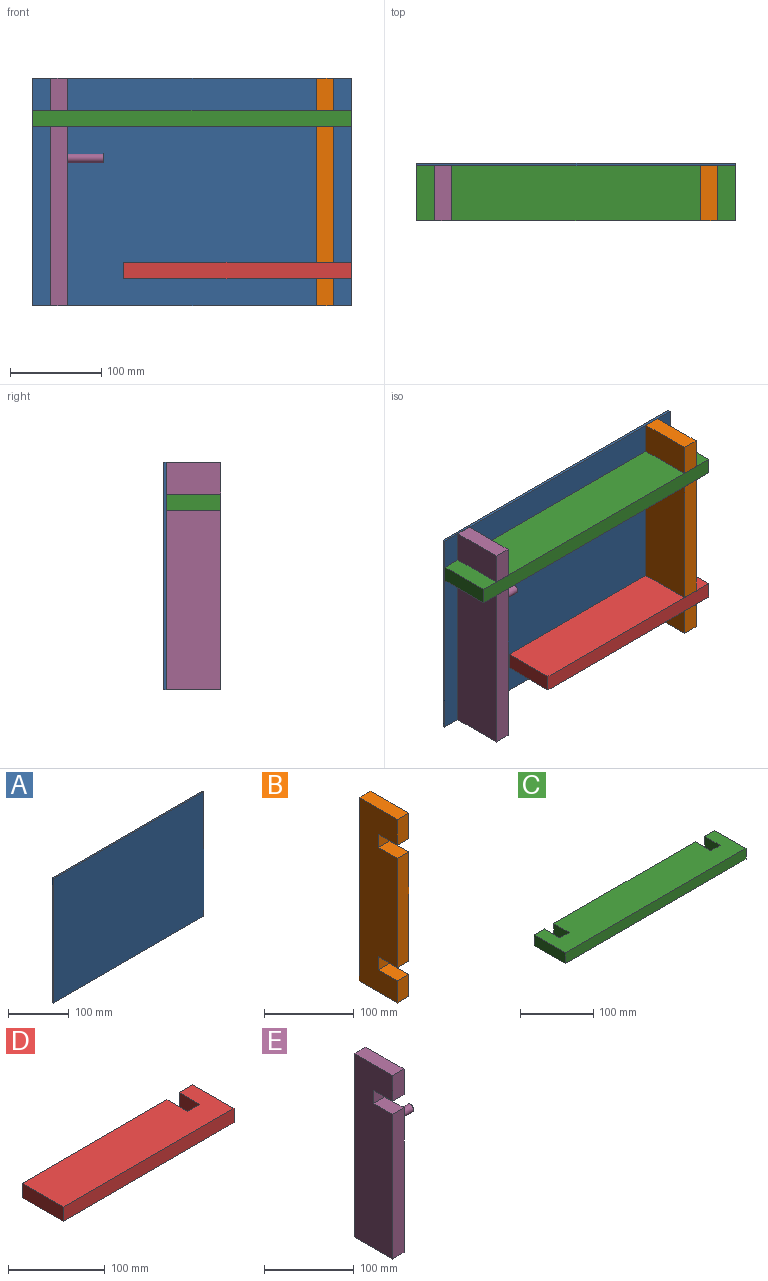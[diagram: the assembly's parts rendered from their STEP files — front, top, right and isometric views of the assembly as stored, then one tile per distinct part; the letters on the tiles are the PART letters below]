
ASSEMBLY  parts=5 mates=4
PART A: 6 faces, bbox 350x3x250 mm
  f0: plane 350x3mm, normal (0,0,1), area 1050mm2, adj f1,f3,f4,f5
  f1: plane 250x3mm, normal (-1,0,0), area 750mm2, adj f0,f2,f4,f5
  f2: plane 350x3mm, normal (0,0,-1), area 1050mm2, adj f1,f3,f4,f5
  f3: plane 250x3mm, normal (1,0,0), area 750mm2, adj f0,f2,f4,f5
  f4: plane 350x250mm, normal (0,-1,0), area 87500mm2, adj f0,f1,f2,f3
  f5: plane 350x250mm, normal (0,1,0), area 87500mm2, adj f0,f1,f2,f3
PART B: 14 faces, bbox 18x60x250 mm
  f0: plane 149x18mm, normal (0,-1,0), area 2682mm2, adj f1,f2,f9,f11
  f1: plane 250x60mm, normal (-1,0,0), area 13920mm2, adj f0,f3,f4,f5,f6,f7,f8,f9
  f2: plane 250x60mm, normal (1,0,0), area 13920mm2, adj f0,f3,f4,f5,f6,f7,f8,f9
  f3: plane 35x18mm, normal (0,-1,0), area 630mm2, adj f1,f2,f4,f8
  f4: plane 60x18mm, normal (0,0,1), area 1080mm2, adj f1,f2,f3,f7
  f5: plane 60x18mm, normal (0,0,-1), area 1080mm2, adj f1,f2,f6,f7
  f6: plane 30x18mm, normal (0,-1,0), area 540mm2, adj f1,f2,f5,f12
  f7: plane 250x18mm, normal (0,1,0), area 4500mm2, adj f1,f2,f4,f5
  f8: plane 30x18mm, normal (0,0,-1), area 540mm2, adj f1,f2,f3,f10
  f9: plane 30x18mm, normal (0,0,1), area 540mm2, adj f0,f1,f2,f10
  f10: plane 18x18mm, normal (0,-1,0), area 324mm2, adj f1,f2,f8,f9
  f11: plane 30x18mm, normal (0,0,-1), area 540mm2, adj f0,f1,f2,f13
  f12: plane 30x18mm, normal (0,0,1), area 540mm2, adj f1,f2,f6,f13
  f13: plane 18x18mm, normal (0,-1,0), area 324mm2, adj f1,f2,f11,f12
PART C: 14 faces, bbox 350x60x18 mm
  f0: plane 20x18mm, normal (0,1,0), area 360mm2, adj f2,f3,f4,f12
  f1: plane 274x18mm, normal (0,1,0), area 4932mm2, adj f2,f3,f8,f11
  f2: plane 350x60mm, normal (0,0,1), area 19920mm2, adj f0,f1,f4,f5,f6,f7,f8,f9
  f3: plane 350x60mm, normal (0,0,-1), area 19920mm2, adj f0,f1,f4,f5,f6,f7,f8,f9
  f4: plane 60x18mm, normal (-1,0,0), area 1080mm2, adj f0,f2,f3,f6
  f5: plane 60x18mm, normal (1,0,0), area 1080mm2, adj f2,f3,f6,f7
  f6: plane 350x18mm, normal (0,-1,0), area 6300mm2, adj f2,f3,f4,f5
  f7: plane 20x18mm, normal (0,1,0), area 360mm2, adj f2,f3,f5,f10
  f8: plane 30x18mm, normal (1,0,0), area 540mm2, adj f1,f2,f3,f9
  f9: plane 18x18mm, normal (0,1,0), area 324mm2, adj f2,f3,f8,f10
  f10: plane 30x18mm, normal (-1,0,0), area 540mm2, adj f2,f3,f7,f9
  f11: plane 30x18mm, normal (-1,0,0), area 540mm2, adj f1,f2,f3,f13
  f12: plane 30x18mm, normal (1,0,0), area 540mm2, adj f0,f2,f3,f13
  f13: plane 18x18mm, normal (0,1,0), area 324mm2, adj f2,f3,f11,f12
PART D: 10 faces, bbox 250x60x18 mm
  f0: plane 212x18mm, normal (0,1,0), area 3816mm2, adj f1,f2,f4,f7
  f1: plane 60x18mm, normal (-1,0,0), area 1080mm2, adj f0,f2,f4,f5
  f2: plane 250x60mm, normal (0,0,-1), area 14460mm2, adj f0,f1,f3,f5,f6,f7,f8,f9
  f3: plane 60x18mm, normal (1,0,0), area 1080mm2, adj f2,f4,f5,f6
  f4: plane 250x60mm, normal (0,0,1), area 14460mm2, adj f0,f1,f3,f5,f6,f7,f8,f9
  f5: plane 250x18mm, normal (0,-1,0), area 4500mm2, adj f1,f2,f3,f4
  f6: plane 20x18mm, normal (0,1,0), area 360mm2, adj f2,f3,f4,f8
  f7: plane 30x18mm, normal (1,0,0), area 540mm2, adj f0,f2,f4,f9
  f8: plane 30x18mm, normal (-1,0,0), area 540mm2, adj f2,f4,f6,f9
  f9: plane 18x18mm, normal (0,1,0), area 324mm2, adj f2,f4,f7,f8
PART E: 12 faces, bbox 58x60x250 mm
  f0: plane 35x18mm, normal (0,-1,0), area 630mm2, adj f1,f2,f3,f7
  f1: plane 250x60mm, normal (-1,0,0), area 14460mm2, adj f0,f3,f4,f5,f6,f7,f8,f9
  f2: plane 250x60mm, normal (1,0,0), area 14381.5mm2, adj f0,f3,f4,f5,f6,f7,f8,f9
  f3: plane 60x18mm, normal (0,0,1), area 1080mm2, adj f0,f1,f2,f6
  f4: plane 60x18mm, normal (0,0,-1), area 1080mm2, adj f1,f2,f5,f6
  f5: plane 197x18mm, normal (0,-1,0), area 3546mm2, adj f1,f2,f4,f8
  f6: plane 250x18mm, normal (0,1,0), area 4500mm2, adj f1,f2,f3,f4
  f7: plane 30x18mm, normal (0,0,-1), area 540mm2, adj f0,f1,f2,f9
  f8: plane 30x18mm, normal (0,0,1), area 540mm2, adj f1,f2,f5,f9
  f9: plane 18x18mm, normal (0,-1,0), area 324mm2, adj f1,f2,f7,f8
  f10: cylinder r=5mm len=40mm, axis (-1,0,0), area 1256.6mm2, adj f2,f11
  f11: plane 10x10mm, normal (1,0,0), area 78.5mm2, adj f10
PLACE A t=(34.73,128.61,58.84)mm
PLACE B t=(64.74,125.61,57.12)mm
PLACE C t=(-82.22,125.61,130.59)mm
PLACE D t=(4605.41,125.61,-43.17)mm
PLACE E t=(-80.26,125.61,57.12)mm
MATE fastened E.f9 <-> C.f13  axis (0,-1,0) through (-121.73,95.61,139.59)mm
MATE fastened B.f10 <-> C.f9  axis (0,-1,0) through (170.27,95.61,139.59)mm
MATE fastened D.f9 <-> B.f13  axis (0,1,0) through (170.27,95.61,-27.41)mm
MATE fastened A.f4 <-> C.f1  axis (0,-1,0) through (24.27,125.61,58.59)mm
